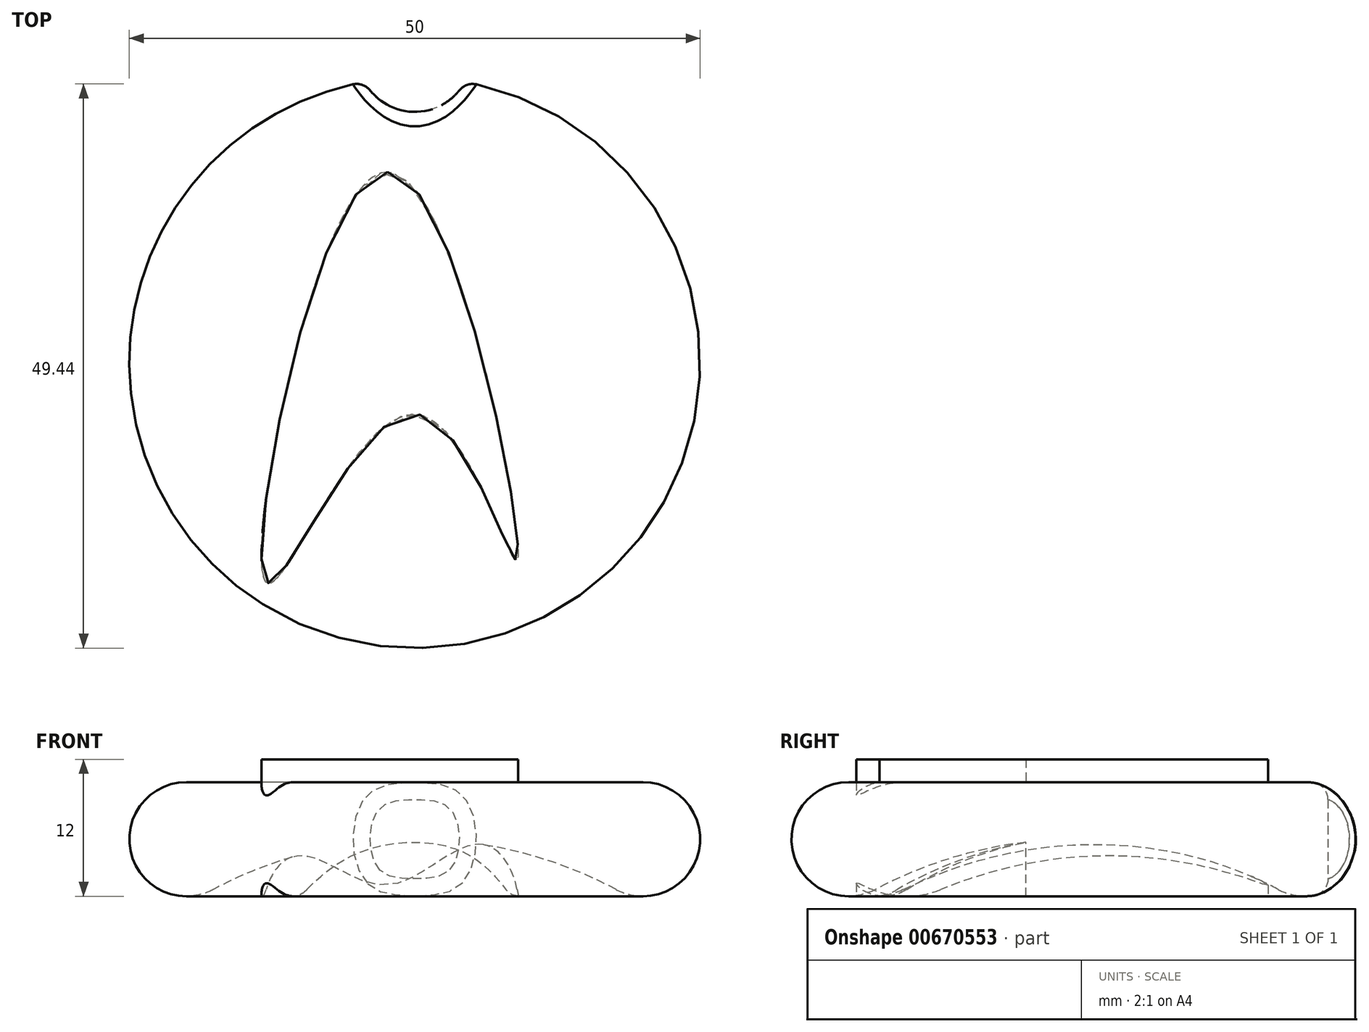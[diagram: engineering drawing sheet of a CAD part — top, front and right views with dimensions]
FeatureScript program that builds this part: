
annotation { "Feature Type Name" : "Feature", "Feature Type Description" : "" }
export const myFeature = defineFeature(function(context is Context, id is Id, definition is map)
    precondition{}
    {
        {
            var Q0;
            Q0=qCreatedBy(makeId("Front.planeOp"),FACE);
            var sketch = newSketch(context, id + "F0", { "sketchPlane" : qUnion([Q0])});
            skArc(sketch, "E0", {"start": v(17.65, -9.41) * mm, "mid": v(9.1, -6.12) * mm, "end": v(0, -5) * mm});
            skArc(sketch, "E1", {"start": v(17.65, -9.41) * mm, "mid": v(24.85, -6.21) * mm, "end": v(20, 0) * mm});
            skLineSegment(sketch, "E2", {"start": v(20, 0) * mm, "end": v(0, 0) * mm});
            skLineSegment(sketch, "E3", {"start": v(0, 0) * mm, "end": v(0, -5) * mm});
            skSolve(sketch);
        }
        {
            var Q0;
            Q0 = qSketchRegion(id + "F0", true);
            var Q1;
            Q1=sQuery(id+"F0.wireOp",EDGE,"E3");
            revolve(context, id + "F1", {"entities" : qUnion([Q0]), "axis" : qUnion([Q1]), "revolveType" : RevolveType.FULL});
        }
        {
            var Q0;
            Q0=qCreatedBy(makeId("Top.planeOp"),FACE);
            cPlane(context, id + "F2", {"entities" : qUnion([Q0]), "cplaneType" : CPlaneType.OFFSET, "offset" : 10 * mm, "oppositeDirection" : true, "width" : 150 * mm, "height" : 150 * mm});
        }
        {
            var Q0;
            Q0=qCreatedBy(id+"F2.planeOp",FACE);
            var sketch = newSketch(context, id + "F3", { "sketchPlane" : qUnion([Q0])});
            skFitSpline(sketch, "E4", {"points": [v(-2.37, 16.75) * mm, v(-12.96, -19.25) * mm, v(0, -4.47) * mm, v(8.95, -17.25) * mm, v(-2.37, 16.75) * mm]});
            skSolve(sketch);
        }
        {
            var Q0;
            Q0 = qSketchRegion(id + "F3", true);
            extrude(context, id + "F4", {"entities" : qUnion([Q0]), "operationType" : NewBodyOperationType.ADD, "depth" : 12 * mm, "offsetDistance" : 25 * mm});
        }
        {
            var Q0;
            Q0=qCreatedBy(id+"F2.planeOp",FACE);
            var sketch = newSketch(context, id + "F5", { "sketchPlane" : qUnion([Q0])});
            skCircle(sketch, "E5", {"center": v(0, 27) * mm, "radius": 5 * mm});
            skSolve(sketch);
        }
        {
            var Q0;
            Q0 = qSketchRegion(id + "F5", true);
            extrude(context, id + "F6", {"entities" : qUnion([Q0]), "operationType" : NewBodyOperationType.REMOVE, "depth" : 25 * mm, "offsetDistance" : 25 * mm});
        }
        {
            var Q0;
            Q0=makeQuery(id+"F6.boolean.opBoolean","INTERSECT",EDGE,{"derivedFrom":[makeQuery(id+"F1.opRevolve","SWEPT_FACE",FACE,{"disambiguationData":[OSD([sQuery(id+"F0.wireOp",EDGE,"E1")])]}),makeQuery(id+"F6.opExtrude","SWEPT_FACE",FACE,{"disambiguationData":[OSD([sQuery(id+"F5.wireOp",EDGE,"E5")])]})]});
            fillet(context, id + "F7", {"entities" : qUnion([Q0]), "radius" : 1.5 * mm, "tangentPropagation" : true, "allowEdgeOverflow" : false});
        }
    });
